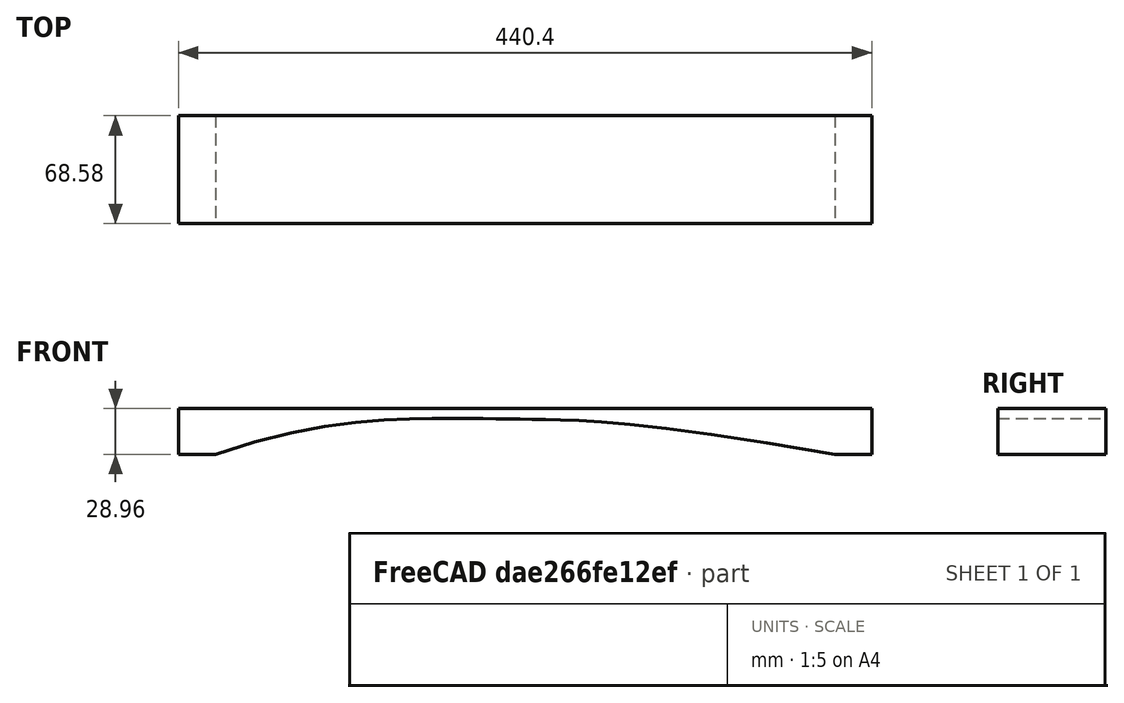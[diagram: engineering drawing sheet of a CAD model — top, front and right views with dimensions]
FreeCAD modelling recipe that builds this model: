
FCSTD DOCUMENT  (FreeCAD 0.20R29410 (Git))
Label: Single_Bar5
License: All rights reserved
LicenseURL: http://en.wikipedia.org/wiki/All_rights_reserved
objects: Fem::FemResultObjectPython×7, Sketcher::SketchObject×1, Part::Extrusion×1, Fem::FemSolverObjectPython×1, App::MaterialObjectPython×1, Fem::ConstraintDisplacement×1, Fem::FemMeshShapeNetgenObject×1, Fem::FemMeshObjectPython×1, App::TextDocument×1, Fem::FemAnalysis×1
note: 2 computed .brp shape members not serialized (recipe doc carries the construction recipe); baked Part::Feature solids carry a one-line shape summary decoded from their .brp

FEATURE [Sketcher::SketchObject] Sketch
  FullyConstrained = true
  Placement = pos=(0,0,0) rot=(1,0,0;1.5708rad)
  sketch-geometry (12):
    g0: LineSegment StartX=23.58 StartY=0 StartZ=0 EndX=0 EndY=0 EndZ=0
    g1: LineSegment StartX=0 StartY=0 StartZ=0 EndX=0 EndY=28.96 EndZ=0
    g2: LineSegment StartX=0 StartY=28.96 StartZ=0 EndX=440.4 EndY=28.96 EndZ=0
    g3: LineSegment StartX=440.4 StartY=28.96 StartZ=0 EndX=440.4 EndY=0 EndZ=0
    g4: LineSegment StartX=440.4 StartY=0 StartZ=0 EndX=416.82 EndY=0 EndZ=0
    g5-g10: Circle x6 (B-spline internal-alignment scaffolding for g11; pole/knot coordinates omitted)
    g11: BSplineCurve PolesCount=6 KnotsCount=4 Degree=3 IsPeriodic=0
  constraints (38):
    c: DistanceX(g0) = 0
    c: DistanceY(g0) = 0
    c: Distance(g1,g1) = 28.96
    c: Distance(g2,g2) = 440.4
    c: DistanceX(g0,g0) = 23.58
    c: DistanceX(g4,g4) = 23.58
    c: Horizontal(g0)
    c: Vertical(g1)
    c: Horizontal(g2)
    c: Vertical(g3)
    c: Horizontal(g4)
    c: Equal(g3,g1)
    c: Coincident(g0,g1)
    c: Coincident(g1,g2)
    c: Coincident(g2,g3)
    c: Coincident(g3,g4)
    c: DistanceX(g6) = 296.03
    c: DistanceY(g6) = 20.95
    c: DistanceX(g7) = 224.26
    c: DistanceY(g7) = 22.21
    c: DistanceX(g8) = 188.45
    c: DistanceY(g8) = 22.89
    c: DistanceX(g9) = 88.83
    c: DistanceY(g9) = 22.5
    c: Weight(g5) = 1
    c: InternalAlignment(g5,g11)
    c: Weight(g6) = 1
    c: InternalAlignment(g6,g11)
    c: Weight(g7) = 1
    c: InternalAlignment(g7,g11)
    c: Weight(g8) = 1
    c: InternalAlignment(g8,g11)
    c: Weight(g9) = 1
    c: InternalAlignment(g9,g11)
    c: Weight(g10) = 1
    c: InternalAlignment(g10,g11)
    c: Coincident(g4,g11)
    c: Coincident(g0,g11)
FEATURE [Part::Extrusion] Bar
  Base = -> Sketch
  Dir = (0,-1,-3e-16)
  DirMode = 2
  FaceMakerClass = Part::FaceMakerBullseye
  LengthFwd = 68.58
  LengthRev = 0
  Solid = true
  Symmetric = false
FEATURE [Fem::FemSolverObjectPython] SolverCcxTools  # FEM object (typed FeaturePython)
  AnalysisType = 1
  BeamShellResultOutput3D = false
  BucklingFactors = 1
  EigenmodeHighLimit = 20000
  EigenmodeLowLimit = 80
  EigenmodesCount = 10
  GeometricalNonlinearity = 0
  IterationsControlParameterCutb = 0.25,0.5,0.75,0.85,,,1.5,
  IterationsControlParameterIter = 4,8,9,200,10,400,,200,,
  IterationsControlParameterTimeUse = false
  IterationsThermoMechMaximum = 2000
  IterationsUserDefinedIncrementations = false
  IterationsUserDefinedTimeStepLength = false
  MaterialNonlinearity = 0
  MatrixSolverType = 0
  SplitInputWriter = false
  ThermoMechSteadyState = false
  TimeEnd = 1
  TimeInitialStep = 0.01
FEATURE [App::MaterialObjectPython] MaterialSolid  # material (typed FeaturePython)
  Category = 0
  Material = CompressiveStrength=4300 kPa; Density=430 kg/m^3; Name=Wood-Chestnut; PoissonRatio=0.32; ShearModulus=7.4 MPa; UltimateTensileStrength=59.0 MPa; YoungsModulus=8500 MPa
FEATURE [Fem::ConstraintDisplacement] FemConstraintDisplacement
  NormalDirection = (0,3e-16,-1)
  Normals = (110) [(0,3.33067e-16,-1),(0,3.33067e-16,-1),(0,3.33067e-16,-1),(0,3.33067e-16,-1),(0,3.33067e-16,-1),(0,3.33067e-16,-1),(0,3.33067e-16,-1),+103 more]
  Points = (110) [(23.58,-68.58,-2.28417e-14),(11.79,-68.58,-2.28417e-14),(0,-68.58,-2.28417e-14),(23.58,-45.72,-1.52278e-14),(11.79,-45.72,-1.52278e-14),+105 more]
  References = -> [Bar]
  rotxFix = false
  rotxFree = true
  rotyFix = false
  rotyFree = true
  rotzFix = false
  rotzFree = true
  xDisplacement = 0
  xFix = false
  xFree = true
  xRotation = 0
  yDisplacement = 0
  yFix = true
  yFree = false
  yRotation = 0
  zDisplacement = 0
  zFix = false
  zFree = true
  zRotation = 0
FEATURE [Fem::FemMeshShapeNetgenObject] FEMMeshNetgen
  Fineness = 4
  GrowthRate = 0.3
  MaxSize = 10
  NbSegsPerEdge = 1
  NbSegsPerRadius = 2
  Optimize = true
  SecondOrder = true
  Shape = -> Bar
FEATURE [Fem::FemMeshObjectPython] ResultMesh  # FEM object (typed FeaturePython)
FEATURE [Fem::FemResultObjectPython] CCX_EigenMode_4_Results  # FEM object (typed FeaturePython)
  DisplacementLengths = [71.236,71.236,97.297,97.297,92.8563,92.8563,104.844,104.844,111.613,111.613,79.3095,79.3095,89.9964,100.75,107.785,105.236,89.7714,74.772,59.7862,44.7638,29.8807,15.2743,4.89891,16.2353,30.712,45.3264,59.6676,73.5919,86.8439,99.1635,+5878 more]
  DisplacementVectors = (5908) [(-29.4481,0,-64.8643),(-29.448,0,-64.8643),(-29.4491,0,-92.7333),(-29.4491,0,-92.7333),(4.77707,0,-92.7333),(4.77703,0,-92.7333),+5902 more]
  Eigenmode = 4
  EigenmodeFrequency = 130.784
  MaxShear = [0.626569,0.647339,0.0217282,0.0250707,0.0753696,0.0552309,0.0865244,0.0997261,0.02234,0.0216753,0.587232,0.588685,0.340789,0.103289,0.0664348,0.0740895,0.118513,0.65265,1.70166,3.59948,6.70028,11.0628,19.3589,31.583,48.0506,71.0386,101.543,+5881 more]
  Mesh = -> ResultMesh
  NodeNumbers = [1,2,3,4,5,6,7,8,9,10,11,12,13,14,15,16,17,18,19,20,21,22,23,24,25,26,27,28,29,30,31,32,33,34,35,36,37,38,39,40,41,42,43,44,45,46,47,48,49,50,51,52,53,54,55,56,57,58,59,60,61,62,63,64,65,66,67,68,69,+5839 more]
  NodeStrainXX = [-0.000126612,-0.000130862,3.52195e-07,8.06703e-07,-4.90433e-07,-2.54052e-07,-8.52058e-07,-6.24987e-07,-5.0251e-08,4.88828e-07,-0.000111157,-0.00011123,-7.23634e-05,-2.06822e-05,-5.02624e-06,6.24394e-06,2.32522e-05,0.000136116,0.000357857,+5889 more]
  NodeStrainXY = [6.13915e-07,-1.68501e-06,-6.57871e-07,3.1917e-07,3.02619e-07,-4.54182e-07,-7.73278e-07,-1.16054e-07,1.14843e-06,-3.95293e-07,1.88229e-06,-3.58879e-06,1.55718e-07,5.89367e-07,-2.32103e-07,-2.86117e-09,-2.43192e-06,-3.53878e-06,-3.75758e-06,+5889 more]
  NodeStrainXZ = [2.1733e-05,2.2194e-05,3.21671e-06,3.81962e-06,1.15542e-05,8.39223e-06,-1.32154e-05,-1.53071e-05,-3.09049e-06,-3.24735e-06,-3.73599e-05,-3.67661e-05,1.52355e-06,4.20564e-06,4.84123e-06,5.02527e-06,1.16988e-06,-3.3871e-06,-9.76041e-07,+5889 more]
  NodeStrainYY = [-6.7167e-07,-5.78026e-07,0,0,-5.56855e-08,-5.31163e-13,8.99686e-08,2.70777e-07,0,0,-2.48911e-07,-4.21882e-07,2.29861e-07,-5.12256e-08,-1.10778e-07,1.14579e-07,-2.00344e-07,-3.14438e-12,1.76562e-12,-2.18435e-11,7.62e-11,7.78688e-11,+5886 more]
  NodeStrainYZ = [-8.45028e-07,2.30892e-07,1.77806e-07,-3.79906e-07,7.29787e-08,-9.46772e-08,6.058e-07,-5.03478e-07,2.54339e-07,-4.30091e-07,-1.54389e-07,3.49742e-07,4.13683e-07,8.10841e-07,-2.94789e-07,-6.92905e-08,-8.24982e-07,-9.1051e-07,-2.56564e-06,+5889 more]
  NodeStrainZZ = [6.30629e-05,6.52101e-05,1.68523e-06,1.73401e-06,-4.16894e-06,-3.64795e-06,-5.16598e-06,-5.22556e-06,1.82335e-06,1.60667e-06,5.51882e-05,5.60427e-05,3.34325e-05,1.01907e-05,1.31813e-05,-1.44562e-05,-1.31838e-05,-6.63708e-05,-0.000170577,+5889 more]
  NodeStressXX = [-1.1829,-1.22177,0.01393,0.0197375,-0.0301466,-0.0239707,-0.0394185,-0.0359626,0.00982545,0.0151422,-1.03756,-1.03455,-0.687497,-0.193527,0.0136787,-0.0061431,0.206213,1.27572,3.37635,7.08439,13.1498,21.9384,37.3398,60.9652,93.703,139.502,+5882 more]
  NodeStressXY = [0.00395324,-0.0108504,-0.00423629,0.00205526,0.00194868,-0.00292466,-0.00497944,-0.000747315,0.00739519,-0.00254544,0.0121208,-0.0231096,0.00100273,0.00379517,-0.0014946,-1.84242e-05,-0.0156601,-0.0227876,-0.0241966,-0.0379258,-0.0946409,+5887 more]
  NodeStressXZ = [0.139947,0.142916,0.0207136,0.024596,0.074402,0.0540409,-0.0850993,-0.0985681,-0.0199009,-0.0209109,-0.240575,-0.236751,0.00981071,0.0270818,0.0311746,0.0323597,0.00753334,-0.0218109,-0.00628511,0.0284388,0.108593,0.386035,6.25487,9.00994,+5884 more]
  NodeStressYY = [-0.371918,-0.382817,0.011662,0.0145428,-0.0273471,-0.0223347,-0.0333524,-0.0301945,0.010149,0.0119945,-0.323386,-0.321017,-0.220041,-0.0606758,0.0453313,-0.0456125,0.0551933,0.399216,1.07197,2.23098,4.12906,6.96609,12.1925,19.5075,29.9653,+5883 more]
  NodeStressYZ = [-0.00544146,0.0014868,0.00114496,-0.00244636,0.000469939,-0.000609664,0.00390098,-0.00324209,0.00163779,-0.00276952,-0.000994168,0.00225213,0.00266387,0.00522132,-0.00189826,-0.000446189,-0.00531238,-0.00586313,-0.0165211,-0.0586114,+5888 more]
  NodeStressZZ = [0.0384946,0.0408186,0.0225139,0.0257087,-0.053834,-0.0458253,-0.0671975,-0.0655876,0.0218903,0.0223405,0.0335952,0.0425802,-0.00623628,0.00527575,0.130924,-0.139439,-0.0284126,-0.0281722,-0.0264368,-0.11259,-0.24649,-0.169352,0.700462,+5885 more]
  PrincipalMax = [0.0543823,0.0567937,0.0394918,0.0475063,0.0334011,0.020401,0.0335148,0.0489301,0.0370241,0.039968,0.0851761,0.0924378,-0.00606151,0.00935963,0.13875,0.0012977,0.208093,1.27667,3.37662,7.0848,13.1517,21.946,38.3797,62.2799,95.0828,140.877,+5882 more]
  PrincipalMed = [-0.371951,-0.382677,0.0125787,0.0151178,-0.0273905,-0.0224709,-0.0339492,-0.0301528,0.0124965,0.0128919,-0.323239,-0.320492,-0.220073,-0.0610674,0.0453042,-0.045611,0.0538332,0.398721,1.07197,2.23214,4.12955,6.96882,12.1912,19.5053,29.9634,+5883 more]
  PrincipalMin = [-1.19875,-1.23789,-0.0039646,-0.00263513,-0.117338,-0.0900607,-0.139534,-0.150522,-0.0076559,-0.00338266,-1.08929,-1.08493,-0.68764,-0.197219,0.00588012,-0.146881,-0.0289325,-0.0286281,-0.0266982,-0.11416,-0.248864,-0.179684,-0.338113,+5885 more]
  ResultType = Fem::ResultMechanical
  Stats = [-29.4491,38.5943,-0.000895095,0.000885243,-104.728,138.265,1.26029,138.265,0.00353546,521.555,-6.70562,586.775,-188.815,188.116,-589.603,7.94768,0.00201691,294.824,0,0,0,0,0,0,0,0]
  Time = 0
  vonMises = [1.10357,1.14033,0.0379898,0.0440361,0.131356,0.0964577,0.151072,0.17396,0.0387558,0.0379292,1.03271,1.03467,0.603726,0.181896,0.118196,0.131174,0.208359,1.15266,3.00841,6.35919,11.8352,19.5571,34.2191,55.8364,84.9583,125.605,179.544,+5881 more]
FEATURE [Fem::FemResultObjectPython] CCX_EigenMode_5_Results  # FEM object (typed FeaturePython)
  DisplacementLengths = [51.9294,51.9293,83.8302,83.8296,82.2549,82.2544,93.1294,93.1293,101.833,101.833,60.7451,60.7449,73.4028,87.2559,95.1632,91.6474,72.1825,51.706,32.3484,18.0791,22.6895,39.8465,59.2979,78.7887,97.6284,115.176,130.381,142.172,149.192,150.092,+5878 more]
  DisplacementVectors = (5908) [(24.146,0,45.9743),(24.1454,0,45.9745),(24.1605,0,80.2731),(24.16,0,80.2726),(-17.9456,0,80.2734),(-17.9451,0,80.273),(-17.1416,0,-91.5382),+5901 more]
  Eigenmode = 5
  EigenmodeFrequency = 533.587
  MaxShear = [8.71081,8.96901,0.308975,0.354603,1.05428,0.77295,1.20335,1.37697,0.318569,0.307905,8.67662,8.69602,5.25145,1.68862,0.951755,1.03327,2.04927,9.66349,23.4788,46.7196,81.9451,128.27,206.909,314.169,442.968,601.196,780.01,956.736,1093.55,1149,+5878 more]
  Mesh = -> ResultMesh
  NodeNumbers = <same value as first occurrence — deduplicated (x7 in doc)>
  NodeStrainXX = [0.00176483,0.00181762,-3.84446e-06,-1.02179e-05,2.16604e-06,3.71845e-07,-2.8133e-06,3.08369e-06,-2.75326e-06,4.82819e-06,-0.00165611,-0.00165774,-0.0011154,-0.000342435,-7.02319e-05,8.50804e-05,0.000408921,0.00202148,0.0049433,0.00979877,+5888 more]
  NodeStrainXY = [-7.81817e-06,2.23695e-05,9.52616e-06,-4.81296e-06,-3.9176e-06,6.23065e-06,-1.0158e-05,-2.22419e-06,1.632e-05,-6.17177e-06,2.65504e-05,-4.87466e-05,2.64354e-06,8.35233e-06,-3.53963e-06,-1.92901e-07,-3.10076e-05,-4.44701e-05,-4.25788e-05,+5889 more]
  NodeStrainXZ = [-0.000293115,-0.000298077,-4.54794e-05,-5.38531e-05,-0.000160939,-0.000116839,-0.000182406,-0.000209618,-4.3518e-05,-4.56965e-05,-0.000533211,-0.00052563,2.58432e-05,6.2491e-05,7.36665e-05,7.44822e-05,2.51481e-05,-2.58133e-05,1.53116e-05,+5889 more]
  NodeStrainYY = [8.70568e-06,7.79056e-06,0,0,6.99444e-07,7.8417e-12,1.26791e-06,3.67611e-06,0,0,-3.59114e-06,-5.62426e-06,2.8846e-06,-8.63315e-07,-1.33621e-06,1.5119e-06,-2.54103e-06,-4.28052e-11,1.79657e-11,-2.62393e-10,7.90099e-10,8.01156e-10,2.59024e-05,+5885 more]
  NodeStrainYZ = [1.1239e-05,-3.26846e-06,-2.3706e-06,5.32187e-06,-1.34725e-06,1.17555e-06,8.68832e-06,-7.99764e-06,3.19505e-06,-5.94284e-06,-3.26954e-06,6.30238e-06,6.30358e-06,1.16464e-05,-4.58071e-06,-1.29804e-06,-1.24613e-05,-1.36019e-05,-3.38802e-05,+5889 more]
  NodeStrainZZ = [-0.000876194,-0.000903223,-2.49396e-05,-2.55027e-05,6.16209e-05,5.36401e-05,-7.82004e-05,-7.99546e-05,2.77721e-05,2.45271e-05,0.000818279,0.000828517,0.000514738,0.000165852,0.000185814,-0.000199163,-0.000222597,-0.000978279,-0.00234801,+5889 more]
  NodeStressXX = [16.5008,16.9829,-0.189513,-0.270259,0.383062,0.311554,-0.474573,-0.399103,0.125476,0.199118,-15.4806,-15.4535,-10.6041,-3.22076,0.201684,-0.0964802,3.68516,18.9882,46.6871,92.239,161.442,254.723,402.908,611.498,869.563,1186.89,1545.43,+5881 more]
  NodeStressXY = [-0.0503443,0.144046,0.0613427,-0.0309926,-0.0252269,0.0401216,-0.0654116,-0.0143224,0.105091,-0.0397424,0.170968,-0.313899,0.0170228,0.0537839,-0.0227931,-0.00124217,-0.19967,-0.28636,-0.274182,-0.400972,-0.968468,-1.1478,1.70827,2.49257,+5884 more]
  NodeStressXZ = [-1.88749,-1.91944,-0.29286,-0.346781,-1.03635,-0.752371,-1.17459,-1.34981,-0.280229,-0.294258,-3.43355,-3.38474,0.166414,0.402404,0.474367,0.47962,0.161939,-0.166222,0.0985975,0.632016,1.63105,4.06448,60.2218,79.92,91.695,99.0619,97.4501,+5881 more]
  NodeStressYY = [5.19237,5.32867,-0.164757,-0.204462,0.373618,0.309159,-0.448293,-0.395288,0.143205,0.168027,-4.83937,-4.81482,-3.40304,-1.02124,0.64533,-0.634611,1.03559,5.97116,14.8552,29.1409,50.8958,80.9848,131.397,195.626,277.974,379.238,492.978,+5881 more]
  NodeStressYZ = [0.0723726,-0.0210469,-0.0152652,0.0342696,-0.00867548,0.00756984,0.0559475,-0.0515,0.0205742,-0.0382683,-0.0210539,0.0405835,0.0405912,0.0749959,-0.029497,-0.00835861,-0.0802433,-0.0875881,-0.218168,-0.685674,-0.895405,-1.6819,0.835558,+5885 more]
  NodeStressZZ = [-0.505844,-0.537708,-0.325353,-0.368684,0.765916,0.654569,-0.960021,-0.933819,0.322041,0.325967,0.452972,0.556545,-0.107016,0.0523041,1.85047,-1.92684,-0.381434,-0.328364,-0.264511,-1.17374,-2.39228,-1.6458,7.02037,3.8458,2.82694,0.938022,+5882 more]
  PrincipalMax = [16.7081,17.1925,0.0581208,0.039413,1.62844,1.25512,0.490001,0.709995,0.525999,0.563617,1.16188,1.24444,-0.103872,0.106859,1.97809,0.0215978,3.70699,18.9959,46.6897,92.2459,161.467,254.795,411.878,621.848,879.168,1195.11,1551.54,1904.46,+5880 more]
  PrincipalMed = [5.19283,5.32689,-0.177914,-0.213024,0.374275,0.310944,-0.456182,-0.394261,0.175861,0.181687,-4.83753,-4.80862,-3.40351,-1.02617,0.644807,-0.634583,1.02389,5.96618,14.856,29.1537,50.9019,81.0103,131.388,195.611,277.964,379.234,492.978,+5881 more]
  PrincipalMin = [-0.713557,-0.745529,-0.559829,-0.669794,-0.480121,-0.290781,-1.91671,-2.04394,-0.111138,-0.0521928,-16.1914,-16.1476,-10.6068,-3.27038,0.0745831,-2.04495,-0.391556,-0.331082,-0.267849,-1.19339,-2.42323,-1.74367,-1.94025,-6.4897,-6.76764,+5883 more]
  ResultType = Fem::ResultMechanical
  Stats = [-17.9458,44.6185,-0.00408389,0.0042916,-114.795,150.57,2.29502,150.752,0.228333,2045.97,-37.6023,2292.51,-745.443,732.588,-2316.11,41.8401,0.12855,1156.55,0,0,0,0,0,0,0,0]
  Time = 0
  vonMises = [15.346,15.8025,0.540108,0.622631,1.83698,1.34969,2.10008,2.40052,0.552679,0.53842,15.2649,15.2921,9.30284,2.97708,1.69206,1.82897,3.60559,17.0728,41.5158,82.5605,144.79,226.784,365.853,555.577,783.39,1063.2,1379.43,1692,1934.07,2032.31,+5878 more]
FEATURE [Fem::FemResultObjectPython] CCX_EigenMode_6_Results  # FEM object (typed FeaturePython)
  DisplacementLengths = [45.3092,45.3083,78.5001,78.5027,74.8915,74.8893,77.1209,77.1205,84.691,84.6903,47.5173,47.5167,58.1635,70.8729,77.6886,74.471,57.134,38.2429,23.0379,21.4678,34.8775,52.0304,69.0299,84.1116,95.845,102.324,101.186,90.0513,67.1145,32.5578,+5878 more]
  DisplacementVectors = (5908) [(-29.254,0,-34.5995),(-29.2513,0,-34.6006),(-29.3366,0,-72.8123),(-29.3392,0,-72.814),(17.5021,0,-72.8177),(17.4998,0,-72.816),(-20.038,0,-74.4722),+5901 more]
  Eigenmode = 6
  EigenmodeFrequency = 1330.02
  MaxShear = [49.7698,51.6258,1.71484,1.96764,5.94755,4.26523,5.93716,6.7667,1.59455,1.53822,44.0338,44.1241,27.1884,8.96174,4.7744,5.10554,11.3132,49.4433,115.394,221.036,372.386,560.488,847.65,1207.03,1578.8,1949.91,2240.24,2334.59,2117.37,1538.57,+5878 more]
  Mesh = -> ResultMesh
  NodeNumbers = <same value as first occurrence — deduplicated (x7 in doc)>
  NodeStrainXX = [-0.0100644,-0.0104856,1.26532e-05,5.14075e-05,4.32467e-05,1.2234e-05,1.12542e-05,4.79096e-05,-1.91296e-05,1.83474e-05,-0.00844012,-0.00844932,-0.00577547,-0.00182618,-0.000347365,0.00041467,0.00227334,0.0103582,0.0243109,0.0464066,+5888 more]
  NodeStrainXY = [4.5029e-05,-0.000119956,-5.82411e-05,2.812e-05,2.27986e-05,-3.38778e-05,-4.83991e-05,-1.26208e-05,8.1428e-05,-3.23331e-05,0.000131424,-0.000236202,1.42528e-05,4.158e-05,-1.83827e-05,-1.36819e-06,-0.000144897,-0.000205705,-0.000182509,+5889 more]
  NodeStrainXZ = [0.0016943,0.00167649,0.000249437,0.000297951,0.000895796,0.000641683,-0.000895405,-0.00102425,-0.000216224,-0.000226946,-0.00265595,-0.00262067,0.000140924,0.000319265,0.000380946,0.000380076,0.000149089,-6.69971e-05,0.000155979,+5889 more]
  NodeStrainYY = [-3.63953e-05,-4.32048e-05,0,0,-3.55813e-06,-4.50344e-11,6.29027e-06,1.78087e-05,0,0,-1.79479e-05,-2.69056e-05,1.33462e-05,-4.61491e-06,-6.04244e-06,7.22538e-06,-1.18375e-05,-2.08082e-10,7.02554e-11,-1.17557e-09,3.14126e-09,3.16378e-09,+5886 more]
  NodeStrainYZ = [-5.56076e-05,1.96152e-05,1.23687e-05,-2.93244e-05,1.29694e-05,-5.79093e-06,4.3551e-05,-4.22104e-05,1.47056e-05,-2.91475e-05,-1.92486e-05,3.5116e-05,3.25573e-05,5.84668e-05,-2.39451e-05,-7.31215e-06,-6.41389e-05,-6.95974e-05,-0.000161509,+5889 more]
  NodeStrainZZ = [0.00501678,0.00519284,0.000143401,0.000145804,-0.000402974,-0.000307616,-0.000403255,-0.000414306,0.000143732,0.000127067,0.00416019,0.00420561,0.0026638,0.000877945,0.000923595,-0.000976906,-0.00121547,-0.00499269,-0.011524,-0.0222236,+5888 more]
  NodeStressXX = [-93.9088,-98.0636,0.974716,1.45985,-1.80093,-1.61196,-2.1353,-1.68678,0.590031,0.950485,-78.9499,-78.8531,-54.925,-17.2135,1.02688,-0.506605,20.6263,97.4118,229.739,437.252,735.58,1114.19,1662.45,2365.43,3117.34,3868.79,4458.12,4656.26,+5880 more]
  NodeStressXY = [0.28996,-0.772442,-0.375037,0.181076,0.146809,-0.218152,-0.311661,-0.0812703,0.524347,-0.208205,0.846289,-1.521,0.0917792,0.26775,-0.118374,-0.00881029,-0.933046,-1.32461,-1.17525,-1.62129,-3.80311,-4.55311,5.88174,7.61783,6.18246,3.09266,+5882 more]
  NodeStressXZ = [10.9102,10.7956,1.60622,1.91862,5.76839,4.13205,-5.76586,-6.59557,-1.39235,-1.4614,-17.1027,-16.8755,0.907468,2.05587,2.45306,2.44746,0.960041,-0.431421,1.00441,3.75593,8.30923,16.3507,223.186,271.392,275.3,249.169,183.463,81.7691,-40.6593,+5879 more]
  NodeStressYY = [-29.3347,-30.8208,0.893237,1.12882,-2.10232,-1.69074,-2.16727,-1.88061,0.713213,0.832339,-24.7162,-24.6178,-17.6486,-5.48375,3.22479,-3.1303,5.91117,30.7115,73.1913,138.421,232.531,354.571,541.569,756.588,996.178,1235.54,1422.04,1485.35,+5880 more]
  NodeStressYZ = [-0.358079,0.12631,0.0796473,-0.188831,0.083515,-0.0372901,0.280442,-0.271809,0.0946951,-0.187692,-0.123949,0.226126,0.209649,0.376491,-0.154192,-0.0470858,-0.413016,-0.448165,-1.04002,-3.01077,-3.73556,-6.68881,3.23278,1.38672,1.50166,+5883 more]
  NodeStressZZ = [3.20474,2.89616,1.81665,2.0677,-4.67432,-3.6716,-4.80449,-4.66317,1.63876,1.65057,2.1884,2.63702,-0.581296,0.199401,9.21109,-9.46751,-1.83948,-1.43842,-1.01598,-4.68493,-8.92035,-6.15962,27.0159,13.2265,8.13123,0.954167,-7.29546,-10.0382,+5880 more]
  PrincipalMax = [4.41846,4.03768,3.06904,3.70658,2.71279,1.62811,2.48604,3.58847,2.62868,2.80344,5.6488,6.00225,-0.563537,0.466408,9.89489,0.11841,20.7282,97.4399,229.752,437.293,735.702,1114.46,1692.39,2396.37,3141.55,3884.78,4465.65,4657.7,4229.26,3077.4,+5878 more]
  PrincipalMed = [-29.3362,-30.8119,0.976206,1.17848,-2.10803,-1.70007,-2.20481,-1.8741,0.873746,0.902954,-24.7077,-24.5902,-17.651,-5.50719,3.22177,-3.13015,5.86816,30.6917,73.1968,138.475,232.558,354.664,541.546,756.552,996.16,1235.54,1422.04,1485.35,+5880 more]
  PrincipalMin = [-95.121,-99.214,-0.360642,-0.228696,-9.18232,-6.90234,-9.38829,-9.94494,-0.560417,-0.272999,-82.4188,-82.2459,-54.9404,-17.4571,0.346093,-10.0927,-1.89833,-1.44671,-1.03478,-4.77957,-9.06953,-6.51963,-2.9058,-17.6804,-16.0575,-15.0342,+5882 more]
  ResultType = Fem::ResultMechanical
  Stats = [-29.3409,40.3353,-0.0129965,0.0170455,-207.273,103.242,0.214099,207.301,1.20688,4544.14,-124.996,5092.29,-1647.45,1629.36,-5138.38,116.904,0.686081,2569.05,0,0,0,0,0,0,0,0]
  Time = 0
  vonMises = [87.6788,90.9787,2.99415,3.45383,10.3629,7.44678,10.3587,11.7926,2.76649,2.68879,77.4854,77.6138,48.1628,15.8072,8.48468,9.03593,19.9135,87.3692,204.062,390.668,658.112,991.042,1499.15,2134.96,2792.64,3448.98,3962.49,4129.49,3745.49,2721.87,+5878 more]
FEATURE [Fem::FemResultObjectPython] CCX_EigenMode_7_Results  # FEM object (typed FeaturePython)
  DisplacementLengths = [40.0846,40.0836,79.8783,80.0687,80.0711,80.068,71.2921,71.2903,79.7746,79.7724,44.6202,44.6188,53.7296,65.9472,71.706,68.0212,50.7941,32.1457,20.7757,27.2302,42.9398,59.0871,72.5022,80.752,81.3596,71.3525,48.7234,19.9228,48.928,104.284,+5878 more]
  DisplacementVectors = (5908) [(27.9562,0,28.7268),(27.9508,0,28.7306),(28.0555,0,74.7892),(28.2313,0,74.9266),(-28.2184,0,74.934),(-28.2131,0,74.9327),(-21.2712,0,-68.0448),+5901 more]
  Eigenmode = 7
  EigenmodeFrequency = 2372.71
  MaxShear = [139.489,163.033,5.49558,6.35064,25.0446,13.6789,16.9631,19.2538,4.58571,4.42004,129.871,130.083,81.7675,27.6475,13.7894,14.5919,34.4377,143.745,325.337,603.081,978.156,1414.49,1996.21,2635.07,3130.48,3379.95,3170.54,2315.98,872.163,1375.73,+5878 more]
  Mesh = -> ResultMesh
  NodeNumbers = <same value as first occurrence — deduplicated (x7 in doc)>
  NodeStrainXX = [0.0267253,0.0331765,9.40265e-05,-0.000150125,-0.00133456,-8.36927e-05,9.94865e-05,0.000222937,-6.79678e-05,3.90606e-05,-0.0249811,-0.0250023,-0.017371,-0.0056574,-0.000990951,0.00117239,0.00694334,0.0301459,0.0685779,0.126731,0.205467,+5887 more]
  NodeStrainXY = [-0.000277716,0.000363974,0.000337598,-9.4077e-05,-0.00015986,0.000103439,-0.00013424,-4.22398e-05,0.000235027,-9.59527e-05,0.000379735,-0.000670024,4.59124e-05,0.000121734,-5.2273e-05,-7.28827e-06,-0.000395834,-0.000555234,-0.000451445,+5889 more]
  NodeStrainXZ = [-0.00647004,-0.00515967,-0.00071926,-0.000958843,-0.00324115,-0.00204744,-0.00254382,-0.0028969,-0.000616528,-0.000648691,-0.00770924,-0.00761456,0.000434769,0.000935351,0.00112962,0.00111494,0.000485013,-4.69904e-05,0.00064501,0.00189911,+5888 more]
  NodeStrainYY = [-0.000225677,0.000129751,0,0,1.31113e-05,1.4162e-10,1.9788e-05,5.44498e-05,0,0,-5.21387e-05,-7.59358e-05,3.59683e-05,-1.73342e-05,-1.47928e-05,1.96801e-05,-3.0736e-05,-6.19221e-10,1.27616e-10,-3.068e-09,7.14574e-09,7.12816e-09,0.000276387,+5885 more]
  NodeStrainYZ = [-2.16223e-05,-6.51017e-05,-3.42618e-05,9.53381e-05,-0.000181508,1.86213e-05,0.000128323,-0.000125914,4.00535e-05,-8.29041e-05,-6.3022e-05,0.000109207,9.425e-05,0.000168179,-7.44467e-05,-2.52699e-05,-0.000189698,-0.000203482,-0.000445933,+5889 more]
  NodeStrainZZ = [-0.0146178,-0.0163928,-0.000484797,-0.000482437,0.00293221,0.00102503,-0.00120379,-0.00123647,0.000426634,0.000375823,0.0122856,0.0123989,0.00800889,0.00270969,0.00264379,-0.00277283,-0.0036771,-0.0144865,-0.0324506,-0.0605141,-0.0982177,+5887 more]
  NodeStressXX = [240.105,310.448,-1.63126,-4.58743,0.62608,4.84921,-5.56705,-4.05413,1.6153,2.62628,-233.829,-233.574,-165.241,-53.4019,2.9949,-1.49857,63.2306,283.754,648.39,1195.09,1936.96,2814.72,3942.11,5199.88,6218.24,6738.92,6329.4,4600.24,1489.48,+5879 more]
  NodeStressXY = [-1.78832,2.34378,2.17393,-0.605799,-1.0294,0.666085,-0.864422,-0.271999,1.51343,-0.617877,2.44526,-4.31455,0.295648,0.783894,-0.336607,-0.046932,-2.54893,-3.57537,-2.90703,-3.74372,-8.49613,-10.346,10.997,11.6415,5.76024,-2.41464,-9.26709,+5881 more]
  NodeStressXZ = [-41.6631,-33.2251,-4.6316,-6.17437,-20.871,-13.1843,-16.3807,-18.6543,-3.97007,-4.17717,-49.6428,-49.0332,2.79965,6.02309,7.27408,7.17955,3.12319,-0.30259,4.15348,12.2291,24.0747,37.5381,463.776,497.176,407.338,237.924,-0.649201,-261.494,+5880 more]
  NodeStressYY = [66.5572,97.6467,-2.23673,-3.62072,9.30428,5.38814,-6.08026,-5.13909,2.05297,2.37476,-73.3019,-73.064,-53.1506,-17.0833,9.28077,-8.92135,18.3218,89.6329,206.789,379.019,613.883,896.569,1282.71,1662.78,1986.31,2150.86,2019.53,1471.42,484.768,+5879 more]
  NodeStressYZ = [-0.139235,-0.419216,-0.220625,0.613919,-1.1688,0.11991,0.826323,-0.810808,0.25792,-0.533852,-0.405823,0.703227,0.606913,1.08297,-0.479392,-0.162723,-1.22154,-1.3103,-2.87154,-7.68904,-8.99776,-15.2109,7.07862,3.02089,3.27671,3.88841,3.4511,+5881 more]
  NodeStressZZ = [-26.1195,-8.74829,-5.35853,-6.72732,28.1015,11.9887,-13.9594,-13.4518,4.80024,4.79483,6.1456,7.26649,-1.80984,0.47713,26.4004,-26.9034,-5.1586,-3.65122,-2.17306,-10.6559,-18.579,-12.9467,59.0065,24.4356,10.5314,-4.20138,-11.6639,-2.05667,+5880 more]
  PrincipalMax = [246.49,313.896,2.32739,0.776754,39.36,22.0837,7.25252,10.4892,7.56147,8.02651,16.0182,16.8923,-1.75461,1.21611,28.4928,0.390824,63.5228,283.82,648.436,1195.23,1937.31,2815.28,3996.78,5247.25,6244.86,6747.31,6329.42,4615.09,1626.71,158.856,+5878 more]
  PrincipalMed = [66.5419,97.6209,-2.89014,-3.78769,9.40108,5.41638,-6.18566,-5.1158,2.517,2.58294,-73.2789,-72.991,-53.1572,-17.1454,9.26925,-8.92109,18.2237,89.5856,206.809,379.151,613.952,896.761,1282.68,1662.74,1986.31,2150.87,2019.52,1471.39,484.764,+5879 more]
  PrincipalMin = [-32.489,-12.1703,-8.66377,-11.9245,-10.7292,-5.27405,-26.6736,-28.0184,-1.60996,-0.813574,-243.725,-243.273,-165.29,-54.0788,0.914025,-28.793,-5.35265,-3.67005,-2.23852,-10.93,-19.0003,-13.6945,4.35826,-22.8947,-16.0874,-12.5931,-11.6698,+5881 more]
  ResultType = Fem::ResultMechanical
  Stats = [-28.2192,41.6558,-0.0735451,0.0550232,-197.409,176.935,1.00923,197.446,7.37101,8176.71,-294.69,8956.43,-2964.8,2874.21,-9236.23,271.43,4.22794,4623.01,0,0,0,0,0,0,0,0]
  Time = 0
  vonMises = [244.967,287.357,9.52268,11.1437,43.656,23.8803,29.5916,33.5476,7.95593,7.72385,228.574,228.868,144.844,48.7788,24.4943,25.8196,60.6287,254.042,575.375,1066.06,1729.03,2501.27,3531.28,4661.78,5538.25,5979.3,5608.49,4095.9,1534.53,2423.18,+5878 more]
FEATURE [Fem::FemResultObjectPython] CCX_EigenMode_8_Results  # FEM object (typed FeaturePython)
  DisplacementLengths = [47.3407,47.3531,61.313,61.3502,87.5905,87.5746,114.448,114.417,75.7144,75.6977,53.043,53.0372,58.5537,66.3967,86.3257,99.8454,106.976,101.422,97.9184,96.3574,96.1223,95.994,94.2753,89.3685,79.6857,65.3704,52.3053,54.7426,73.8835,91.9284,+5878 more]
  DisplacementVectors = (5908) [(44.813,0,-15.2623),(44.8273,0,-15.2587),(44.6064,0,-42.066),(44.8288,0,-41.8835),(76.9144,0,-41.9079),(76.9052,0,-41.8916),(-99.6217,0,-56.3361),+5901 more]
  Eigenmode = 8
  EigenmodeFrequency = 3453.77
  MaxShear = [85.6654,63.4101,6.94631,7.72436,19.0078,15.7167,29.3531,32.7282,8.38926,8.13966,76.419,72.2502,25.4907,21.2499,24.6992,26.2959,142.021,404.366,752.864,1207.16,1755.98,2342.09,2996.24,3589.94,3896.03,3795.35,3154.08,2007.94,739.355,587.955,+5878 more]
  Mesh = -> ResultMesh
  NodeNumbers = <same value as first occurrence — deduplicated (x7 in doc)>
  NodeStrainXX = [-0.01874,-0.0128292,0.000192214,0.000178271,-0.00132766,9.39603e-05,0.000161478,0.000276555,-7.7089e-05,9.67985e-05,-0.0150493,-0.013979,-0.00512455,0.00408312,-0.00182594,0.00216085,0.0295153,0.0850911,0.158897,0.254282,0.36985,0.493951,+5886 more]
  NodeStrainXY = [-0.000147017,-0.000343889,-4.59205e-05,0.000120341,-0.000102491,-0.000153503,-0.000251199,-8.65613e-05,0.00040899,-0.000170025,0.000288688,-0.000465977,4.06225e-05,0.000237055,-3.30789e-05,-5.78545e-05,-0.000671312,-0.000782964,+5890 more]
  NodeStrainXZ = [-8.08213e-05,0.00156214,0.0010588,0.00116572,0.00278072,0.00235645,-0.00440587,-0.00495111,-0.00114281,-0.00120023,-0.0036825,-0.00387035,0.00123226,0.00156577,0.00195784,0.00194136,0.000973991,0.000185616,0.00108035,0.00254048,0.00450159,+5887 more]
  NodeStrainYY = [-0.000461481,-0.000117707,0,0,2.556e-05,-2.64903e-10,1.25546e-05,0.000133803,0,0,2.01639e-06,-8.98945e-06,5.65159e-05,-3.36819e-05,-9.71517e-06,4.23497e-05,-2.68912e-05,-1.27059e-09,-3.22288e-10,-3.82806e-09,6.22482e-09,6.12415e-09,+5886 more]
  NodeStrainYZ = [-0.000388033,-2.3495e-05,5.33981e-05,-9.62637e-05,-0.000118325,6.41987e-07,0.000230441,-0.000173419,7.96239e-05,-0.000159412,-0.000119123,0.000153901,8.54248e-06,0.000269075,-0.000177161,-3.00206e-05,-0.000296735,-0.0002604,-0.000595724,+5889 more]
  NodeStrainZZ = [0.0078469,0.00660631,0.000566777,0.000605252,0.000624494,-0.0011361,-0.00204866,-0.00199156,0.000782992,0.000672384,0.00750567,0.00706269,0.00239883,-0.00168192,0.00476356,-0.00502257,-0.0145307,-0.0404906,-0.074916,-0.120597,-0.175445,+5887 more]
  NodeStressXX = [-185.667,-118.905,5.58213,5.63277,-12.4279,-5.36004,-9.69035,-7.26982,3.54412,5.02605,-140.076,-129.656,-48.2772,39.8443,5.00112,-2.22326,275.677,803.224,1503.9,2402.62,3494.37,4672.38,5982.78,7154.35,7779.06,7572.3,6262.77,3900.64,1113.93,+5879 more]
  NodeStressXY = [-0.946699,-2.21444,-0.2957,0.774923,-0.659982,-0.988465,-1.61757,-0.557402,2.63365,-1.09486,1.85898,-3.00061,0.261584,1.52649,-0.213008,-0.372548,-4.32285,-5.04181,-4.17221,-4.17034,-8.84698,-9.86939,7.24404,3.98445,-3.78885,-10.7925,+5882 more]
  NodeStressXZ = [-0.52044,10.0592,6.81805,7.50653,17.9062,15.1741,-28.3711,-31.8822,-7.35902,-7.72874,-23.7131,-24.9227,7.935,10.0826,12.6073,12.5012,6.27191,1.19525,6.95681,16.3592,28.9875,37.4707,382.013,322.873,136.22,-105.261,-347.134,-506.878,-505.002,+5879 more]
  NodeStressYY = [-67.9643,-37.0509,4.34439,4.48481,-3.71395,-5.96509,-10.6493,-8.18906,4.04052,4.40273,-43.1545,-39.6975,-14.9143,13.3346,16.6965,-15.8651,85.4433,255.289,480.698,765.2,1112.76,1491.63,1931.97,2285.05,2484.05,2417.67,2003.74,1256.41,371.592,+5879 more]
  NodeStressYZ = [-2.4987,-0.151294,0.343851,-0.61988,-0.76194,0.00413401,1.4839,-1.11672,0.51273,-1.02652,-0.767082,0.991027,0.0550084,1.73268,-1.14081,-0.193315,-1.91079,-1.67682,-3.8361,-8.35845,-9.15211,-14.338,6.69074,2.52704,3.2529,2.56127,0.347822,+5881 more]
  NodeStressZZ = [-14.4633,6.2477,7.99409,8.38227,0.142822,-13.2809,-23.9223,-21.8751,9.08252,8.73248,5.16446,5.8398,0.168778,2.72089,47.4335,-48.4802,-7.95257,-5.44653,-1.71537,-11.3697,-16.997,-11.0248,39.2453,3.57771,-8.23841,-15.4495,-7.03729,14.8313,+5880 more]
  PrincipalMax = [-14.3455,7.05348,13.7126,14.6389,12.8954,6.41112,12.6491,18.138,14.2937,14.8287,8.95916,10.3237,1.4359,42.5306,50.9357,0.948998,275.916,803.272,1503.95,2402.74,3494.64,4672.71,6007.25,7168.9,7781.44,7573.78,6281.96,3965.68,1313.34,130.365,+5878 more]
  PrincipalMed = [-68.0727,-36.9951,4.38808,4.67069,-3.77411,-5.99487,-10.8539,-8.15355,4.85833,4.78321,-43.1464,-39.6608,-14.9131,13.3385,16.6581,-15.8748,85.3785,255.253,480.711,765.278,1112.8,1491.73,1931.98,2285.05,2484.05,2417.65,2003.71,1256.41,+5880 more]
  PrincipalMin = [-185.676,-119.767,-0.180045,-0.809777,-25.1203,-25.0223,-46.0571,-47.3184,-2.48485,-1.45063,-143.879,-134.177,-49.5456,0.0307173,1.53733,-51.6428,-8.12642,-5.45899,-1.77771,-11.5699,-17.3092,-11.4598,14.7724,-10.9735,-10.6249,-16.9118,+5882 more]
  ResultType = Fem::ResultMechanical
  Stats = [-99.6425,76.947,-0.0848924,0.0605984,-85.5415,102.587,2.5765,114.498,8.29849,11474,-191.235,12962.4,-939.09,4180.33,-2895.39,301.519,4.77615,6487.49,0,0,0,0,0,0,0,0]
  Time = 0
  vonMises = [151.775,111.523,12.2641,13.5658,33.0054,27.4227,51.1765,57.0511,14.5682,14.2265,134.576,127.106,45.0877,37.6531,43.8395,46.5204,250.726,714.962,1331.73,2134.68,3105.17,4142.44,5300.63,6351.16,6892.1,6713.1,5577.5,3547.87,1296.5,1032.13,+5878 more]
FEATURE [Fem::FemResultObjectPython] CCX_EigenMode_9_Results  # FEM object (typed FeaturePython)
  DisplacementLengths = [68.3168,68.3232,91.0011,91.0282,62.3257,62.3424,52.3526,52.4429,89.8053,89.9094,76.5512,76.5333,78.8781,83.4508,76.7468,63.1797,37.2873,26.7552,26.9355,37.1542,50.0953,61.5663,68.8563,69.6391,63.5375,55.3673,62.9218,95.3046,135.71,164.1,+5878 more]
  DisplacementVectors = (5908) [(-66.5111,0,-15.603),(-66.5143,0,-15.6174),(-67.3319,0,-61.2178),(-67.3423,0,-61.2466),(-11.5983,0,-61.237),(-11.5967,0,-61.2543),+5902 more]
  Eigenmode = 9
  EigenmodeFrequency = 3686.61
  MaxShear = [412.516,418.827,11.3696,12.0226,36.2599,26.9352,24.4549,30.1545,7.33637,7.06075,296.022,309.777,198.757,85.289,21.5405,20.385,10.3801,132.4,393.207,797.809,1309.65,1851.87,2434.4,2890.7,2861.7,2166.52,764.981,2085.35,4815.62,6965.03,7565.6,+5877 more]
  Mesh = -> ResultMesh
  NodeNumbers = <same value as first occurrence — deduplicated (x7 in doc)>
  NodeStrainXX = [-0.0841256,-0.0854948,3.23359e-05,0.000246564,0.000435495,0.000308639,3.27043e-05,0.000542593,-0.000315341,-8.7196e-06,-0.0558851,-0.0596803,-0.0423966,-0.0181419,-0.00139135,0.00149007,0.001393,0.0277215,0.0825179,0.167558,0.275172,+5887 more]
  NodeStrainXY = [0.000396569,-0.000671331,-0.000294819,0.000172208,0.000286054,-0.000105566,-4.81963e-05,-1.38695e-05,0.000520624,-0.000182184,0.000564603,-0.00140845,5.50793e-05,0.000212436,-0.000385961,0.000140278,-0.000402203,-0.000803935,-0.000353231,+5889 more]
  NodeStrainXZ = [0.0132985,0.0132838,0.00166832,0.00180738,0.00544502,0.00398353,-0.00368867,-0.00448932,-0.000884319,-0.00101597,-0.0190364,-0.0180473,0.000427833,0.00147269,0.00190432,0.00173822,0.000765618,0.000253566,0.00129469,0.00402686,0.00723065,+5887 more]
  NodeStrainYY = [-0.000426721,-0.000190754,0,0,-0.000119768,-3.81631e-11,0.000155562,-6.24473e-05,0,0,-7.63107e-05,-0.000183595,0.000122945,4.29943e-05,-8.59881e-05,-3.85005e-05,-0.000101317,-2.53523e-10,1.01773e-09,-4.82e-09,1.06917e-08,1.08464e-08,+5886 more]
  NodeStrainYZ = [-0.000327087,0.000264125,6.20061e-05,-0.00022278,4.26142e-05,-8.66968e-05,0.000166118,-0.000287321,4.00552e-05,-0.000111179,2.49475e-05,0.000248589,0.000507992,0.000365496,5.79721e-05,-0.000119284,-0.000338406,-0.000438587,-0.000618438,+5889 more]
  NodeStrainZZ = [0.0412019,0.0418392,0.000970616,0.000909822,-0.00236961,-0.00222426,-0.00173519,-0.00206111,0.000655699,0.000651218,0.0277964,0.0294667,0.0193157,0.0081642,0.00401658,-0.00378892,-0.00125774,-0.0133598,-0.039569,-0.0800502,-0.131288,+5887 more]
  NodeStressXX = [-789.852,-801.507,5.94902,8.20677,-8.95191,-8.97738,-8.64387,-5.55534,-0.0824307,3.62145,-521.08,-558.295,-404.417,-173.688,5.57493,-3.78365,9.16431,260.714,777.201,1579.86,2595.52,3684.88,4815.46,5728.89,5712.28,4309.45,1092.73,-3840.76,+5880 more]
  NodeStressXY = [2.55367,-4.32296,-1.89846,1.10892,1.84201,-0.679783,-0.310355,-0.089311,3.3525,-1.17315,3.6357,-9.06955,0.354677,1.36796,-2.48535,0.903307,-2.58994,-5.17685,-2.2746,-5.24786,-11.0587,-14.8008,11.3055,6.71809,-4.33526,-13.9391,-16.8152,+5881 more]
  NodeStressXZ = [85.6345,85.5397,10.7429,11.6384,35.0626,25.6515,-23.7528,-28.9085,-5.69448,-6.54224,-122.583,-116.214,2.75499,9.48323,12.2627,11.1931,4.93011,1.63281,8.33704,25.9305,46.561,52.8127,578.616,492.597,219.204,-151.824,-530.044,-792.284,+5880 more]
  NodeStressYY = [-250.882,-252.2,5.7408,6.61905,-12.5275,-10.9648,-7.85274,-9.45143,1.94818,3.6776,-161.705,-175.173,-130.618,-56.5883,13.9807,-13.6267,-0.458168,82.2049,245.836,500.887,823.578,1173.76,1570.03,1833.62,1823.58,1373.2,349.031,-1217.25,+5880 more]
  NodeStressYZ = [-2.10624,1.70081,0.399282,-1.43457,0.27441,-0.558275,1.0697,-1.85017,0.257931,-0.715922,0.160647,1.60077,3.27116,2.35358,0.373305,-0.768119,-2.17913,-2.82424,-3.98236,-12.5277,-13.6728,-22.135,9.87312,4.45604,2.93172,3.93977,1.55949,+5881 more]
  NodeStressZZ = [17.1813,18.4473,11.991,12.4777,-27.0151,-25.2877,-20.0281,-22.3216,6.17048,7.87105,17.7785,15.7567,-7.02805,-4.29264,40.3987,-37.7772,-7.90484,-3.8239,-8.96459,-14.5875,-21.836,-16.8682,86.2901,32.0704,5.70449,-12.8543,-10.0103,17.1641,+5880 more]
  PrincipalMax = [26.18,27.2815,20.1776,22.1849,18.3092,9.82122,10.135,16.2032,9.84617,12.6263,44.3557,38.4424,-6.92232,-3.65218,44.2886,-0.397631,11.2927,260.875,777.3,1580.31,2596.42,3685.72,4885.27,5771.18,5720.69,4314.84,1306.46,173.538,113.049,67.2107,+5878 more]
  PrincipalMed = [-250.88,-252.17,6.0649,6.97894,-12.5931,-11.0018,-7.88483,-9.4258,3.01662,4.03906,-161.673,-175.042,-130.704,-56.6866,14.458,-13.6222,-1.02404,82.1445,245.887,501.159,823.72,1174.07,1570.03,1833.62,1823.58,1373.14,348.798,-1217.23,-3002.25,+5879 more]
  PrincipalMin = [-798.853,-810.372,-2.56163,-1.86032,-54.2106,-44.0493,-38.7749,-44.1058,-4.82656,-1.49523,-547.689,-581.112,-404.437,-174.23,1.20771,-41.1677,-9.46739,-3.92461,-9.11444,-15.3089,-22.8785,-18.0248,16.4794,-10.2182,-2.70855,-18.1892,-223.505,+5881 more]
  ResultType = Fem::ResultMechanical
  Stats = [-67.3478,77.1731,-0.054725,0.0448839,-167.153,150.537,8.82772,169.782,7.61619,14310.6,-448.474,8067.28,-5204.4,2637.22,-16158,418.708,3.99829,8092.23,0,0,0,0,0,0,0,0]
  Time = 0
  vonMises = [727.226,738.696,19.8828,21.0657,63.0321,47.0519,42.8432,52.4248,12.7171,12.3245,520.563,545.122,352.327,151.205,38.2191,36.0267,18.0828,233.957,694.936,1410.2,2315.16,3274.69,4307.52,5115.11,5063.6,3831.75,1338.92,3678.1,8512.45,12317.9,+5878 more]
FEATURE [Fem::FemResultObjectPython] CCX_EigenMode_10_Results  # FEM object (typed FeaturePython)
  DisplacementLengths = [36.7972,36.7064,81.6208,81.4718,82.3042,82.1742,70.2088,78.3401,76.0171,84.1124,44.2147,44.3785,49.0605,60.7034,66.5378,63.6593,49.256,33.4306,31.9864,44.2172,58.9236,68.1618,66.9806,52.3785,28.4466,45.1001,98.5052,148.021,169.365,143.377,+5878 more]
  DisplacementVectors = (5908) [(-33.9256,0,-14.2509),(-33.8378,0,-14.2255),(-35.1754,0,-73.6522),(-35.1349,0,-73.5064),(36.7019,0,-73.6679),(36.605,0,-73.5709),(30.1249,0,63.4174),+5901 more]
  Eigenmode = 10
  EigenmodeFrequency = 5085.92
  MaxShear = [696.369,722.429,20.0408,29.782,81.8969,55.0511,101.048,75.243,93.7959,21.5411,567.596,590.057,431.701,145.56,109.778,85.9016,59.4647,80.8544,1137.65,2450.68,3610.07,4682.75,5459.9,5617.12,4541.44,2241.02,2545.29,6357.16,8760.52,7873.48,+5878 more]
  Mesh = -> ResultMesh
  NodeNumbers = <same value as first occurrence — deduplicated (x7 in doc)>
  NodeStrainXX = [-0.141959,-0.147255,-0.000126966,0.000420904,0.00120854,0.000646794,0.013549,-0.000742777,0.00971625,0.00011983,-0.0812658,0.113847,-0.080618,-0.0190722,-0.00490761,0.00657791,0.00220399,0.0123431,-0.214505,-0.515902,-0.76061,-0.987331,+5886 more]
  NodeStrainXY = [-0.000877213,-0.0020819,-0.00136017,0.000670889,-0.00137603,-0.00132732,-0.00828364,-0.000259608,-0.0124204,0.000630122,0.0158864,0.00212063,0.000201484,-0.00673927,0.0145813,-0.00479795,-0.00641801,-0.000929362,-0.0171699,0.00163934,+5888 more]
  NodeStrainXZ = [0.0215079,0.0205952,0.00249136,0.00440882,0.0119474,0.0081814,-0.00567368,0.0113257,-0.00557301,0.00306808,0.0731119,0.0334796,-0.00391563,0.00737519,-0.00546477,0.00190388,0.00636639,0.00225025,0.0132668,-0.00996962,-0.0170166,-0.0131595,+5886 more]
  NodeStrainYY = [0.000776791,-0.00165403,0,0,0.000882428,-3.08822e-09,-0.0103503,0.00107147,0,0,-0.00508999,0.000211027,-0.00513784,8.96361e-05,0.00231444,0.00479453,0.000862763,1.46022e-08,5.19664e-09,9.02141e-09,-1.74687e-08,-2.01221e-08,0.000192447,+5885 more]
  NodeStrainYZ = [-0.00145994,-0.000449411,0.000182623,-2.15588e-05,0.000553483,0.000504377,-0.00188003,0.00116433,-0.000689451,0.000276944,-0.00904725,-0.000870163,-0.0132152,-0.00467071,-0.00580002,0.00774037,0.000892905,0.00187715,-0.00924338,0.00343387,+5888 more]
  NodeStrainZZ = [0.0699675,0.073276,0.00212713,0.00277861,-0.00701237,-0.0034709,-0.000666397,0.00447759,-0.000314492,-0.00203105,0.0120823,-0.0566869,0.0502423,0.0203895,0.00206238,-0.0118142,-0.00110449,-0.0120055,0.135806,0.244937,0.360077,0.466751,+5886 more]
  NodeStressXX = [-1321.75,-1381.15,10.6312,21.0241,-20.3873,-12,101.741,22.7277,116.382,-10.168,-948.437,1061.5,-722.407,-114.76,-34.6402,39.8293,25.4242,81.4144,-1831.75,-4873.07,-7190.47,-9337.56,-10932.2,-11241.8,-9006.55,-3796.4,4036.46,12345.5,17405.8,+5879 more]
  NodeStressXY = [-5.64872,-13.4062,-8.7587,4.32012,-8.8608,-8.54716,-53.3416,-1.67172,-79.98,4.0576,102.299,13.6556,1.29744,-43.3968,93.8949,-30.8959,-41.3281,-5.98453,-110.564,10.5563,16.7918,23.9472,-5.6664,15.5491,35.3326,33.6526,17.7318,-16.7824,+5880 more]
  NodeStressXZ = [138.498,132.621,16.0428,28.3901,76.9342,52.6833,-36.535,72.9308,-35.8868,19.7566,470.797,215.589,-25.2143,47.4917,-35.1898,12.2599,40.9957,14.4902,85.4302,-64.1983,-109.576,-84.7393,-700.425,-251.074,435.57,1155.29,1559.55,1431.42,679.979,+5879 more]
  NodeStressYY = [-402.623,-443.57,11.4488,18.3137,-22.4873,-16.165,-52.1554,34.4103,53.8148,-10.9397,-457.911,329.748,-236.361,8.63035,11.8654,28.3454,16.7875,1.93237,-450.464,-1550.98,-2292.61,-2979.75,-3529.55,-3603.35,-2873.85,-1212.79,1277.33,3912.19,+5880 more]
  NodeStressYZ = [-9.40114,-2.89393,1.17598,-0.138825,3.56409,3.24788,-12.1062,7.49758,-4.43965,1.78335,-58.2588,-5.60332,-85.0976,-30.0765,-37.3486,49.8433,5.74977,12.0877,-59.5218,22.112,22.4225,37.8797,-18.9086,-8.71849,5.42812,-3.13326,1.66324,18.5741,+5880 more]
  NodeStressZZ = [42.9227,38.9345,25.1462,36.2063,-73.325,-38.5155,10.2031,56.3436,51.7897,-24.0184,-347.331,-36.6402,120.254,139.349,10.2423,-78.6046,4.11952,-75.3761,424.046,26.271,26.0713,25.8503,-102.732,-18.8501,34.2471,43.6841,13.5095,-42.1924,+5880 more]
  PrincipalMax = [57.0508,51.248,36.1147,58.1629,34.9676,29.5664,126.977,114.669,177.014,5.02403,-89.3201,1102.51,140.237,157.605,111.227,69.8253,74.5009,83.0367,431.896,27.4179,27.9464,27.0889,-57.5194,-13.2131,55.2009,364.481,4570.31,12508.8,17432.4,+5879 more]
  PrincipalMed = [-402.814,-443.424,15.0784,18.7822,-22.3409,-15.7111,7.93131,34.629,55.5499,-12.0919,-439.847,329.709,-255.587,9.1303,-15.431,21.7228,16.2587,3.60597,-446.663,-1551.25,-2292.76,-2980.13,-3529.64,-3603.34,-2873.67,-1212.43,1277.25,3912.27,+5880 more]
  PrincipalMin = [-1335.69,-1393.61,-3.96694,-1.40102,-128.826,-80.5358,-75.1193,-35.8167,-10.5776,-38.0582,-1224.51,-77.6075,-723.164,-133.516,-108.328,-101.978,-44.4284,-78.672,-1843.4,-4873.95,-7192.19,-9338.42,-10977.3,-11247.4,-9027.69,-4117.55,+5882 more]
  ResultType = Fem::ResultMechanical
  Stats = [-45.1648,36.7019,-2.03964,2.91541,-183.24,172.783,1.48179,183.305,34.726,47438.5,-15002.9,52794.3,-22975.7,21710.8,-52979.7,15834.1,20.0408,27049.1,0,0,0,0,0,0,0,0]
  Time = 0
  vonMises = [1229.12,1271.84,34.726,52.4694,143.965,95.8508,175.943,130.413,164.799,37.5718,1006.78,1038.22,748.588,252.135,190.888,153.512,103.003,140.051,1987.43,4333.35,6384.38,8282.03,9663.48,9938.04,8029.6,3937.96,4471.54,11236.3,15495.1,13931.5,+5878 more]
FEATURE [App::TextDocument] ccx_dat_file
  Text = <blob: 4861 chars omitted>
FEATURE [Fem::FemAnalysis] Analysis
  Group = -> [SolverCcxTools,MaterialSolid,FemConstraintDisplacement,FEMMeshNetgen,CCX_EigenMode_4_Results,CCX_EigenMode_5_Results,CCX_EigenMode_6_Results,CCX_EigenMode_7_Results,CCX_EigenMode_8_Results,CCX_EigenMode_9_Results,CCX_EigenMode_10_Results,ccx_dat_file]
